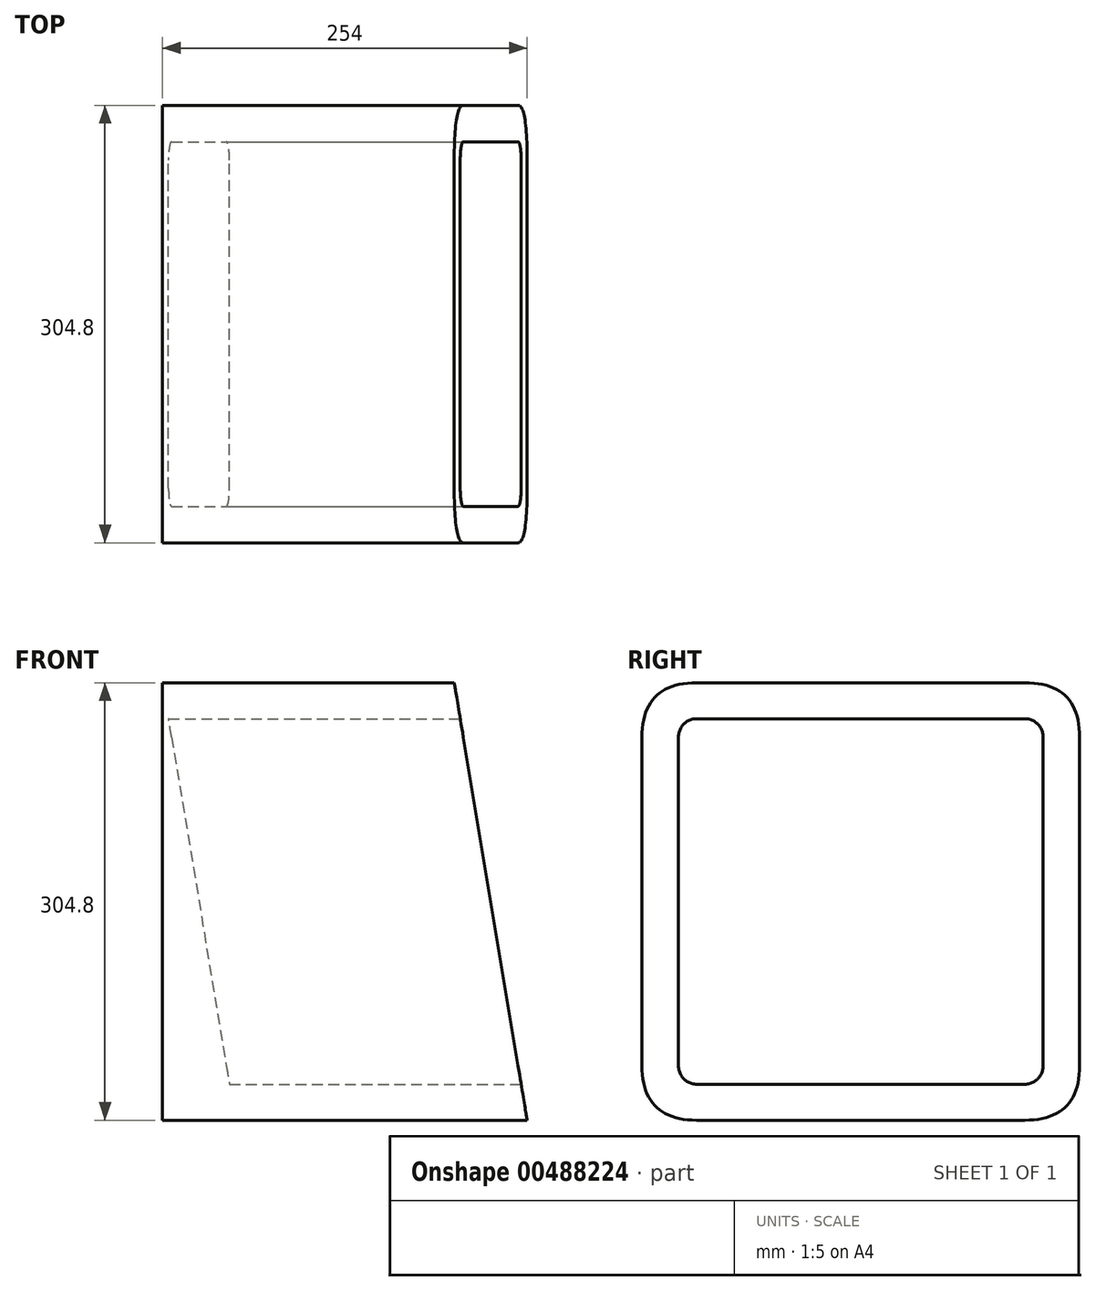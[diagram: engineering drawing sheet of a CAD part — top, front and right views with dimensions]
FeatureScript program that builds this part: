
annotation { "Feature Type Name" : "Feature", "Feature Type Description" : "" }
export const myFeature = defineFeature(function(context is Context, id is Id, definition is map)
    precondition{}
    {
        {
            var Q0;
            Q0=qCreatedBy(makeId("Front.planeOp"),FACE);
            var sketch = newSketch(context, id + "F0", { "sketchPlane" : qUnion([Q0])});
            skLineSegment(sketch, "E0.bottom", {"start": v(-152.4, 152.4) * mm, "end": v(152.4, 152.4) * mm});
            skLineSegment(sketch, "E0.top", {"start": v(-152.4, -152.4) * mm, "end": v(152.4, -152.4) * mm});
            skLineSegment(sketch, "E0.left", {"start": v(-152.4, 152.4) * mm, "end": v(-152.4, -152.4) * mm});
            skLineSegment(sketch, "E0.right", {"start": v(152.4, 152.4) * mm, "end": v(152.4, -152.4) * mm});
            skPoint(sketch, "E0.middle", {"position": v(0, 0) * mm});
            skSolve(sketch);
        }
        {
            var Q0;
            Q0=makeQuery(id+"F0.imprint","IMPRINT",FACE,{"disambiguationData":[TD([[makeQuery(id+"F0.imprint","IMPRINT",EDGE,{"derivedFrom":sQuery(id+"F0.wireOp",EDGE,"E0.bottom")}),-1.0]])]});
            extrude(context, id + "F1", {"entities" : qUnion([Q0]), "depth" : 304.8 * mm});
        }
        {
            var Q0;
            Q0=makeQuery(id+"F1.opExtrude","CAP_FACE",FACE,{"disambiguationData":[OSD([sQuery(id+"F0.wireOp",EDGE,"E0.bottom"),sQuery(id+"F0.wireOp",EDGE,"E0.top"),sQuery(id+"F0.wireOp",EDGE,"E0.left"),sQuery(id+"F0.wireOp",EDGE,"E0.right")])],"isStart":false});
            var sketch = newSketch(context, id + "F2", { "sketchPlane" : qUnion([Q0])});
            skLineSegment(sketch, "E1", {"start": v(50.8, 152.4) * mm, "end": v(101.6, -152.4) * mm});
            skLineSegment(sketch, "E2", {"start": v(101.6, -152.4) * mm, "end": v(152.4, -152.4) * mm});
            skLineSegment(sketch, "E3", {"start": v(152.4, -152.4) * mm, "end": v(152.4, 152.4) * mm});
            skLineSegment(sketch, "E4", {"start": v(152.4, 152.4) * mm, "end": v(50.8, 152.4) * mm});
            skSolve(sketch);
        }
        {
            var Q0;
            Q0 = qSketchRegion(id + "F2", true);
            extrude(context, id + "F3", {"entities" : qUnion([Q0]), "operationType" : NewBodyOperationType.REMOVE, "endBound" : BoundingType.THROUGH_ALL, "oppositeDirection" : true, "depth" : 25.4 * mm});
        }
        {
            var Q0;
            Q0=makeQuery(id+"F1.opExtrude","CAP_EDGE",EDGE,{"disambiguationData":[OSD([sQuery(id+"F0.wireOp",EDGE,"E0.bottom")])],"isStart":false});
            var Q1;
            Q1=makeQuery(id+"F1.opExtrude","CAP_EDGE",EDGE,{"disambiguationData":[OSD([sQuery(id+"F0.wireOp",EDGE,"E0.bottom")])],"isStart":true});
            var Q2;
            Q2=makeQuery(id+"F1.opExtrude","CAP_EDGE",EDGE,{"disambiguationData":[OSD([sQuery(id+"F0.wireOp",EDGE,"E0.top")])],"isStart":true});
            var Q3;
            Q3=makeQuery(id+"F1.opExtrude","CAP_EDGE",EDGE,{"disambiguationData":[OSD([sQuery(id+"F0.wireOp",EDGE,"E0.top")])],"isStart":false});
            fillet(context, id + "F4", {"entities" : qUnion([Q0, Q1, Q2, Q3]), "radius" : 38.1 * mm, "tangentPropagation" : true, "rho" : .5, "crossSection" : FilletCrossSection.CONIC, "allowEdgeOverflow" : false});
        }
        {
            var Q0;
            Q0=makeQuery(id+"F3.boolean.opBoolean","COPY",FACE,{"derivedFrom":makeQuery(id+"F3.opExtrude","SWEPT_FACE",FACE,{"disambiguationData":[OSD([sQuery(id+"F2.wireOp",EDGE,"E1")])]})});
            var sketch = newSketch(context, id + "F5", { "sketchPlane" : qUnion([Q0])});
            skLineSegment(sketch, "E5.0.0", {"start": v(-266.7, -167.03) * mm, "end": v(-38.1, -167.03) * mm});
            skFitSpline(sketch, "E5.0.1", {"points": [v(-38.1, -167.03) * mm, v(-12.7, -167.03) * mm, v(0, -154.15) * mm, v(0, -128.4) * mm]});
            skLineSegment(sketch, "E5.0.2", {"start": v(0, -128.4) * mm, "end": v(0, 103.35) * mm});
            skFitSpline(sketch, "E5.0.3", {"points": [v(0, 103.35) * mm, v(0, 129.1) * mm, v(-12.7, 141.97) * mm, v(-38.1, 141.97) * mm]});
            skLineSegment(sketch, "E5.0.4", {"start": v(-38.1, 141.97) * mm, "end": v(-266.7, 141.97) * mm});
            skFitSpline(sketch, "E5.0.5", {"points": [v(-266.7, 141.97) * mm, v(-292.1, 141.97) * mm, v(-304.8, 129.1) * mm, v(-304.8, 103.35) * mm]});
            skLineSegment(sketch, "E5.0.6", {"start": v(-304.8, 103.35) * mm, "end": v(-304.8, -128.4) * mm});
            skFitSpline(sketch, "E5.0.7", {"points": [v(-304.8, -128.4) * mm, v(-304.8, -154.15) * mm, v(-292.1, -167.03) * mm, v(-266.7, -167.03) * mm]});
            skLineSegment(sketch, "E6", {"start": v(-266.7, 141.97) * mm, "end": v(-38.1, -167.03) * mm, "construction": true});
            skLineSegment(sketch, "E7", {"start": v(-266.7, -167.03) * mm, "end": v(-38.1, 141.97) * mm, "construction": true});
            skLineSegment(sketch, "E8.bottom", {"start": v(-279.4, 116.57) * mm, "end": v(-25.4, 116.57) * mm});
            skLineSegment(sketch, "E8.top", {"start": v(-279.4, -141.63) * mm, "end": v(-25.4, -141.63) * mm});
            skLineSegment(sketch, "E8.left", {"start": v(-279.4, 116.57) * mm, "end": v(-279.4, -141.63) * mm});
            skLineSegment(sketch, "E8.right", {"start": v(-25.4, 116.57) * mm, "end": v(-25.4, -141.63) * mm});
            skPoint(sketch, "E8.middle", {"position": v(-152.4, -12.53) * mm});
            skSolve(sketch);
        }
        {
            var Q0;
            Q0=makeQuery(id+"F5.imprint","IMPRINT",FACE,{"disambiguationData":[TD([[makeQuery(id+"F5.imprint","IMPRINT",EDGE,{"derivedFrom":sQuery(id+"F5.wireOp",EDGE,"E8.bottom")}),-1.0]])]});
            var Q1;
            {var subQ0=sQuery(id+"F0.wireOp",EDGE,"E0.bottom");Q1=makeQuery(id+"F4.opFillet","BLEND_EDGE",EDGE,{"blendedFrom":[makeQuery(id+"F1.opExtrude","CAP_EDGE",EDGE,{"disambiguationData":[OSD([subQ0])],"isStart":false}),makeQuery(id+"F1.opExtrude","SWEPT_FACE",FACE,{"disambiguationData":[OSD([subQ0])]})],"blendedInto":[makeQuery(id+"F1.opExtrude","SWEPT_FACE",FACE,{"disambiguationData":[OSD([subQ0])]})]});}
            sweep(context, id + "F6", {"operationType" : NewBodyOperationType.REMOVE, "profiles" : qUnion([Q0]), "path" : qUnion([Q1])});
        }
        {
            var Q0;
            Q0=makeQuery(id+"F6.boolean.opBoolean","COPY",EDGE,{"derivedFrom":makeQuery(id+"F6.opSweep","SWEPT_EDGE",EDGE,{"disambiguationData":[OSD([sQuery(id+"F0.wireOp",EDGE,"E0.bottom"),sQuery(id+"F5.wireOp",EDGE,"E8.bottom"),sQuery(id+"F5.wireOp",EDGE,"E8.left")])]})});
            var Q1;
            Q1=makeQuery(id+"F6.boolean.opBoolean","COPY",EDGE,{"derivedFrom":makeQuery(id+"F6.opSweep","SWEPT_EDGE",EDGE,{"disambiguationData":[OSD([sQuery(id+"F0.wireOp",EDGE,"E0.bottom"),sQuery(id+"F5.wireOp",EDGE,"E8.top"),sQuery(id+"F5.wireOp",EDGE,"E8.left")])]})});
            var Q2;
            Q2=makeQuery(id+"F6.boolean.opBoolean","COPY",EDGE,{"derivedFrom":makeQuery(id+"F6.opSweep","SWEPT_EDGE",EDGE,{"disambiguationData":[OSD([sQuery(id+"F0.wireOp",EDGE,"E0.bottom"),sQuery(id+"F5.wireOp",EDGE,"E8.top"),sQuery(id+"F5.wireOp",EDGE,"E8.right")])]})});
            var Q3;
            Q3=makeQuery(id+"F6.boolean.opBoolean","COPY",EDGE,{"derivedFrom":makeQuery(id+"F6.opSweep","SWEPT_EDGE",EDGE,{"disambiguationData":[OSD([sQuery(id+"F0.wireOp",EDGE,"E0.bottom"),sQuery(id+"F5.wireOp",EDGE,"E8.bottom"),sQuery(id+"F5.wireOp",EDGE,"E8.right")])]})});
            fillet(context, id + "F7", {"entities" : qUnion([Q0, Q1, Q2, Q3]), "radius" : 12.7 * mm, "tangentPropagation" : true, "allowEdgeOverflow" : false});
        }
    });
